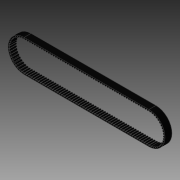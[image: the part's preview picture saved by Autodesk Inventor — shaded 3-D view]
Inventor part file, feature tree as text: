
AUTODESK INVENTOR PART (.ipt)
format: ipt  version: 2014 SP1 (Build 180222100, 222)  size: 1,420,288 bytes
history: native  units: in
note: dims shown in document units (in); Inventor stores cm internally (conversion verified against a paired STEP export)
features: extrude x2, sketch x1, pattern_linear x1
ambient origin geometry x8: Origin, YZ Plane, XZ Plane, XY Plane, X Axis, Y Axis, Z Axis, Center Point
bodies: Solid1 (feature_tree)
feature tree (4):
  sketch  "Sketch1"  dims[d0=1.29in d1=10.5507in d2=1.3315in d3=0.5906in d4=0.0in d6=58.2677in d8=0.0039in d9=0.0681in d10=0.5906in d11=0.0in]
  extrude  "Extrusion1"  Depth=10.5507in
  pattern_linear  "Rectangular Pattern1"  Spacing1=1.3315in  [1 undecoded]
  extrude  "Extrusion2"  Depth=0.5906in TaperAngle=0.0deg
note: 1 required parameter value undecoded (feature->parameter linkage not recoverable at this tier; creation-order binding heuristic only, values carry confidence <= 0.55)
